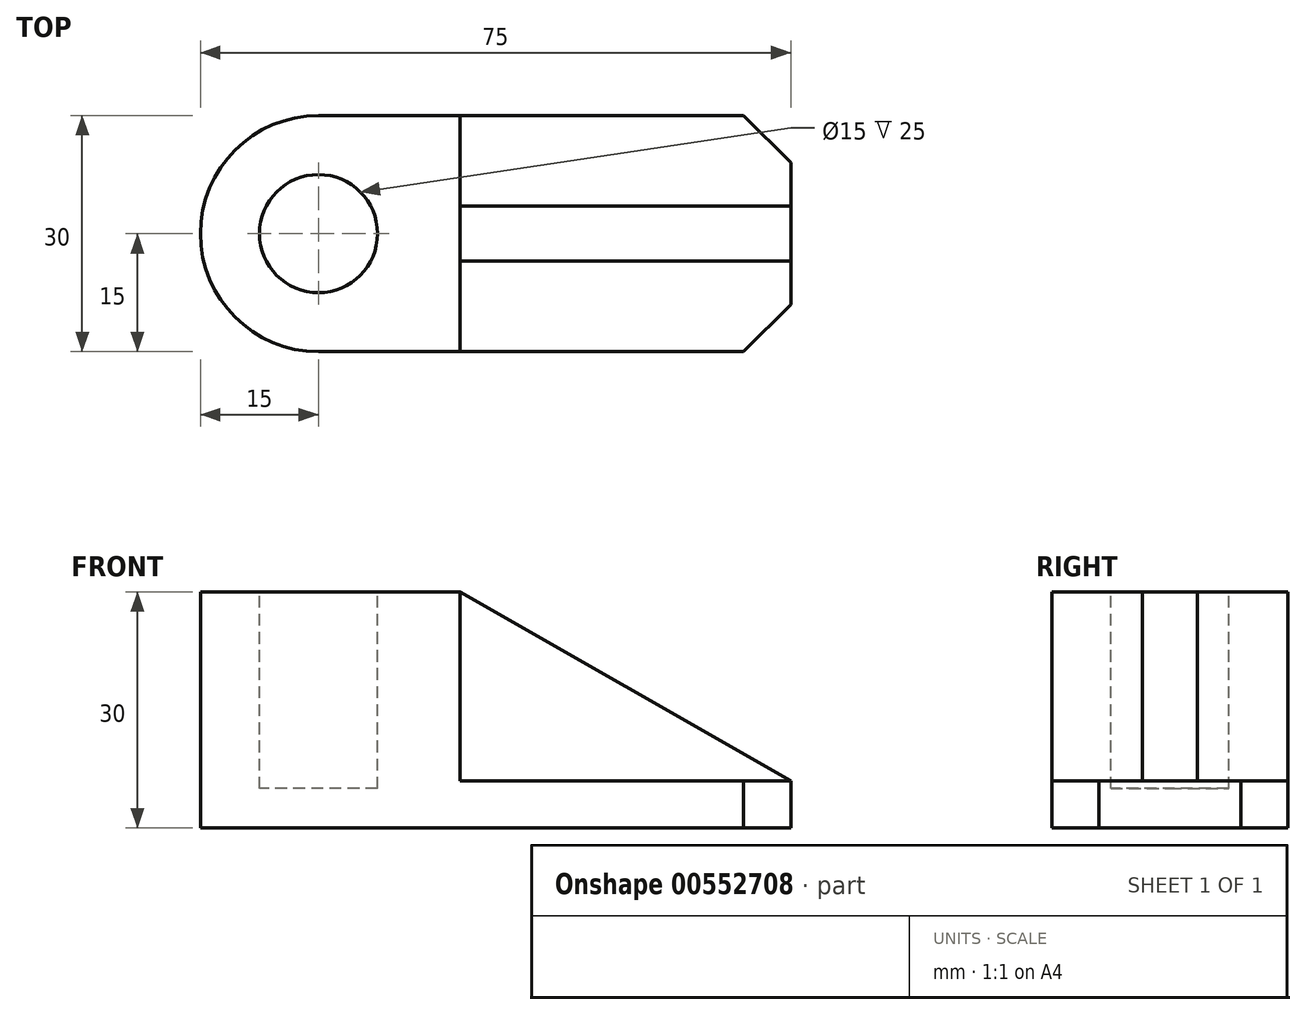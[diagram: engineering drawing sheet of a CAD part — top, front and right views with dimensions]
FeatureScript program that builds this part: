
annotation { "Feature Type Name" : "Feature", "Feature Type Description" : "" }
export const myFeature = defineFeature(function(context is Context, id is Id, definition is map)
    precondition{}
    {
        {
            var Q0;
            Q0=qCreatedBy(makeId("Front.planeOp"),FACE);
            var sketch = newSketch(context, id + "F0", { "sketchPlane" : qUnion([Q0])});
            skLineSegment(sketch, "E0.bottom", {"start": v(-30, 7.28) * mm, "end": v(30, 7.28) * mm});
            skLineSegment(sketch, "E0.top", {"start": v(-30, -22.72) * mm, "end": v(30, -22.72) * mm});
            skLineSegment(sketch, "E0.left", {"start": v(-30, 7.28) * mm, "end": v(-30, -22.72) * mm});
            skLineSegment(sketch, "E0.right", {"start": v(30, 7.28) * mm, "end": v(30, -22.72) * mm});
            skSolve(sketch);
        }
        {
            var Q0;
            Q0=makeQuery(id+"F0.imprint","IMPRINT",FACE,{"disambiguationData":[TD([[makeQuery(id+"F0.imprint","IMPRINT",EDGE,{"derivedFrom":sQuery(id+"F0.wireOp",EDGE,"E0.bottom")}),-1.0]])]});
            extrude(context, id + "F1", {"entities" : qUnion([Q0]), "depth" : 30 * mm, "offsetDistance" : 25 * mm});
        }
        {
            var Q0;
            Q0=makeQuery(id+"F1.opExtrude","SWEPT_FACE",FACE,{"disambiguationData":[OSD([sQuery(id+"F0.wireOp",EDGE,"E0.bottom")])]});
            var sketch = newSketch(context, id + "F2", { "sketchPlane" : qUnion([Q0])});
            skArc(sketch, "E1", {"start": v(-30, 0) * mm, "mid": v(-45, -15) * mm, "end": v(-30, -30) * mm});
            skLineSegment(sketch, "E2", {"start": v(-30, -30) * mm, "end": v(-30, 0) * mm, "construction": true});
            skSolve(sketch);
        }
        {
            var Q0;
            Q0=makeQuery(id+"F2.imprint","IMPRINT",FACE,{"disambiguationData":[TD([[makeQuery(id+"F2.imprint","IMPRINT",EDGE,{"derivedFrom":sQuery(id+"F2.wireOp",EDGE,"E1")}),1.0]])]});
            extrude(context, id + "F3", {"entities" : qUnion([Q0]), "operationType" : NewBodyOperationType.ADD, "oppositeDirection" : true, "depth" : 30 * mm, "offsetDistance" : 25 * mm});
        }
        {
            var Q0;
            {var subQ0=sQuery(id+"F0.wireOp",EDGE,"E0.bottom");Q0=makeQuery(id+"F3.boolean.opBoolean","MERGE",FACE,{"derivedFrom":[makeQuery(id+"F1.opExtrude","SWEPT_FACE",FACE,{"disambiguationData":[OSD([subQ0])]}),makeQuery(id+"F3.opExtrude","CAP_FACE",FACE,{"disambiguationData":[OSD([subQ0,sQuery(id+"F0.wireOp",EDGE,"E0.left"),sQuery(id+"F2.wireOp",EDGE,"E1")])],"isStart":true})]});}
            var sketch = newSketch(context, id + "F4", { "sketchPlane" : qUnion([Q0])});
            skLineSegment(sketch, "E3.bottom", {"start": v(30, -30) * mm, "end": v(-12, -30) * mm});
            skLineSegment(sketch, "E3.top", {"start": v(30, 0) * mm, "end": v(-12, 0) * mm});
            skLineSegment(sketch, "E3.left", {"start": v(30, -30) * mm, "end": v(30, 0) * mm});
            skLineSegment(sketch, "E3.right", {"start": v(-12, -30) * mm, "end": v(-12, 0) * mm});
            skSolve(sketch);
        }
        {
            var Q0;
            Q0=makeQuery(id+"F4.imprint","IMPRINT",FACE,{"disambiguationData":[TD([[makeQuery(id+"F4.imprint","IMPRINT",EDGE,{"derivedFrom":sQuery(id+"F4.wireOp",EDGE,"E3.bottom")}),1.0]])]});
            extrude(context, id + "F5", {"entities" : qUnion([Q0]), "operationType" : NewBodyOperationType.REMOVE, "oppositeDirection" : true, "depth" : 24 * mm, "offsetDistance" : 25 * mm});
        }
        {
            var Q0;
            Q0=makeQuery(id+"F5.boolean.opBoolean","COPY",FACE,{"derivedFrom":makeQuery(id+"F5.opExtrude","SWEPT_FACE",FACE,{"disambiguationData":[OSD([sQuery(id+"F4.wireOp",EDGE,"E3.right")])]})});
            var sketch = newSketch(context, id + "F6", { "sketchPlane" : qUnion([Q0])});
            skLineSegment(sketch, "E4.bottom", {"start": v(-18.5, 7.28) * mm, "end": v(-11.5, 7.28) * mm});
            skLineSegment(sketch, "E4.top", {"start": v(-18.5, -16.72) * mm, "end": v(-11.5, -16.72) * mm});
            skLineSegment(sketch, "E4.left", {"start": v(-18.5, 7.28) * mm, "end": v(-18.5, -16.72) * mm});
            skLineSegment(sketch, "E4.right", {"start": v(-11.5, 7.28) * mm, "end": v(-11.5, -16.72) * mm});
            skSolve(sketch);
        }
        {
            var Q0;
            Q0=makeQuery(id+"F6.imprint","IMPRINT",FACE,{"disambiguationData":[TD([[makeQuery(id+"F6.imprint","IMPRINT",EDGE,{"derivedFrom":sQuery(id+"F6.wireOp",EDGE,"E4.bottom")}),-1.0]])]});
            var Q1;
            Q1=makeQuery(id+"F1.opExtrude","SWEPT_FACE",FACE,{"disambiguationData":[OSD([sQuery(id+"F0.wireOp",EDGE,"E0.right")])]});
            extrude(context, id + "F7", {"entities" : qUnion([Q0]), "operationType" : NewBodyOperationType.ADD, "endBound" : BoundingType.UP_TO_SURFACE, "depth" : 25 * mm, "endBoundEntityFace" : qUnion([Q1]), "offsetDistance" : 25 * mm});
        }
        {
            var Q0;
            Q0=makeQuery(id+"F7.opExtrude","SWEPT_FACE",FACE,{"disambiguationData":[OSD([sQuery(id+"F6.wireOp",EDGE,"E4.left")])]});
            var sketch = newSketch(context, id + "F8", { "sketchPlane" : qUnion([Q0])});
            skLineSegment(sketch, "E5", {"start": v(-12, 7.28) * mm, "end": v(30, -16.72) * mm});
            skSolve(sketch);
        }
        {
            var Q0;
            Q0=makeQuery(id+"F8.imprint","IMPRINT",FACE,{"disambiguationData":[TD([[makeQuery(id+"F8.imprint","IMPRINT",EDGE,{"derivedFrom":sQuery(id+"F8.wireOp",EDGE,"E5")}),1.0]])]});
            extrude(context, id + "F9", {"entities" : qUnion([Q0]), "operationType" : NewBodyOperationType.REMOVE, "oppositeDirection" : true, "depth" : 25 * mm, "offsetDistance" : 25 * mm});
        }
        {
            var Q0;
            {var subQ0=sQuery(id+"F0.wireOp",EDGE,"E0.bottom");Q0=makeQuery(id+"F7.boolean.opBoolean","MERGE",FACE,{"derivedFrom":[makeQuery(id+"F3.boolean.opBoolean","MERGE",FACE,{"derivedFrom":[makeQuery(id+"F1.opExtrude","SWEPT_FACE",FACE,{"disambiguationData":[OSD([subQ0])]}),makeQuery(id+"F3.opExtrude","CAP_FACE",FACE,{"disambiguationData":[OSD([subQ0,sQuery(id+"F0.wireOp",EDGE,"E0.left"),sQuery(id+"F2.wireOp",EDGE,"E1")])],"isStart":true})]}),makeQuery(id+"F7.opExtrude","SWEPT_FACE",FACE,{"disambiguationData":[OSD([sQuery(id+"F6.wireOp",EDGE,"E4.bottom")])]})]});}
            var sketch = newSketch(context, id + "F10", { "sketchPlane" : qUnion([Q0])});
            skCircle(sketch, "E6", {"center": v(-30, -15) * mm, "radius": 7.5 * mm});
            skSolve(sketch);
        }
        {
            var Q0;
            Q0=makeQuery(id+"F10.imprint","IMPRINT",FACE,{"disambiguationData":[TD([[makeQuery(id+"F10.imprint","IMPRINT",EDGE,{"derivedFrom":sQuery(id+"F10.wireOp",EDGE,"E6")}),1.0]])]});
            extrude(context, id + "F11", {"entities" : qUnion([Q0]), "operationType" : NewBodyOperationType.REMOVE, "oppositeDirection" : true, "depth" : 25 * mm, "offsetDistance" : 25 * mm});
        }
        {
            var Q0;
            Q0=makeQuery(id+"F1.opExtrude","CAP_EDGE",EDGE,{"disambiguationData":[OSD([sQuery(id+"F0.wireOp",EDGE,"E0.right")])],"isStart":false});
            var Q1;
            Q1=makeQuery(id+"F1.opExtrude","CAP_EDGE",EDGE,{"disambiguationData":[OSD([sQuery(id+"F0.wireOp",EDGE,"E0.right")])],"isStart":true});
            chamfer(context, id + "F12", {"entities" : qUnion([Q0, Q1]), "width" : 6 * mm, "tangentPropagation" : true});
        }
    });
